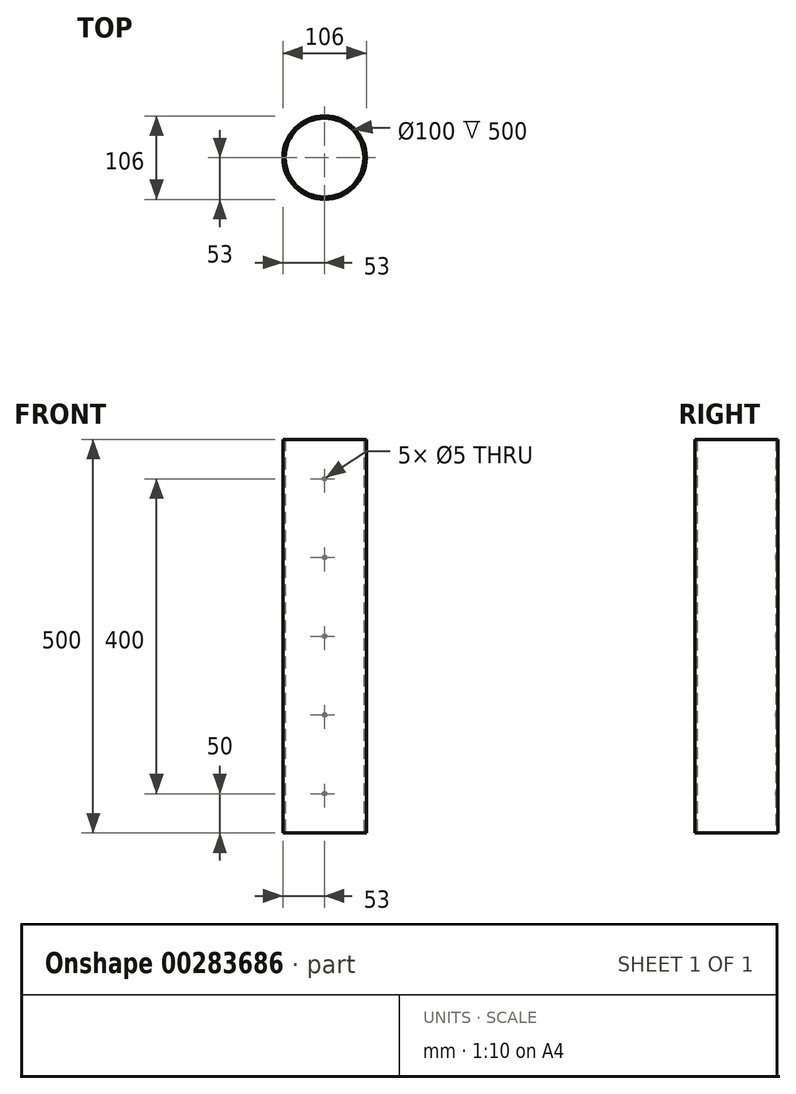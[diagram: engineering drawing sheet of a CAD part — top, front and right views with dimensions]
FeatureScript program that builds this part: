
annotation { "Feature Type Name" : "Feature", "Feature Type Description" : "" }
export const myFeature = defineFeature(function(context is Context, id is Id, definition is map)
    precondition{}
    {
        {
            var Q0;
            Q0=qCreatedBy(makeId("Top.planeOp"),FACE);
            var sketch = newSketch(context, id + "F0", { "sketchPlane" : qUnion([Q0])});
            skCircle(sketch, "E0", {"center": v(0, 0) * mm, "radius": 50 * mm});
            skCircle(sketch, "E1", {"center": v(0, 0) * mm, "radius": 53 * mm});
            skSolve(sketch);
        }
        {
            var Q0;
            Q0=makeQuery(id+"F0.imprint","IMPRINT",FACE,{"disambiguationData":[TD([[makeQuery(id+"F0.imprint","IMPRINT",EDGE,{"derivedFrom":sQuery(id+"F0.wireOp",EDGE,"E0")}),-1.0]])]});
            extrude(context, id + "F1", {"entities" : qUnion([Q0]), "depth" : 500 * mm});
        }
        {
            var Q0;
            Q0=qCreatedBy(makeId("Front.planeOp"),FACE);
            var sketch = newSketch(context, id + "F2", { "sketchPlane" : qUnion([Q0])});
            skPoint(sketch, "E2", {"position": v(0, 450) * mm});
            skPoint(sketch, "E3", {"position": v(0, 350) * mm});
            skPoint(sketch, "E4", {"position": v(0, 250) * mm});
            skPoint(sketch, "E5", {"position": v(0, 150) * mm});
            skPoint(sketch, "E6", {"position": v(0, 50) * mm});
            skSolve(sketch);
        }
        {
            var Q0;
            Q0=sQuery(id+"F2.wireOp",VERTEX,"E2");
            var Q1;
            Q1=sQuery(id+"F2.wireOp",VERTEX,"E3");
            var Q2;
            Q2=sQuery(id+"F2.wireOp",VERTEX,"E4");
            var Q3;
            Q3=sQuery(id+"F2.wireOp",VERTEX,"E5");
            var Q4;
            Q4=sQuery(id+"F2.wireOp",VERTEX,"E6");
            var Q5;
            Q5=makeQuery(id+"F1.opExtrude","SWEPT_BODY",BODY,{"disambiguationData":[OSD([sQuery(id+"F0.wireOp",EDGE,"E0"),sQuery(id+"F0.wireOp",EDGE,"E1")])]});
            hole(context, id + "F3", {"style" : HoleStyle.SIMPLE, "endStyle" : HoleEndStyle.THROUGH, "holeDiameter" : 5 * mm, "isTappedThrough" : true, "tappedDepth" : 12 * mm, "tapClearance" : 3, "startFromSketch" : true, "locations" : qUnion([Q0, Q1, Q2, Q3, Q4]), "scope" : qUnion([Q5])});
        }
    });
